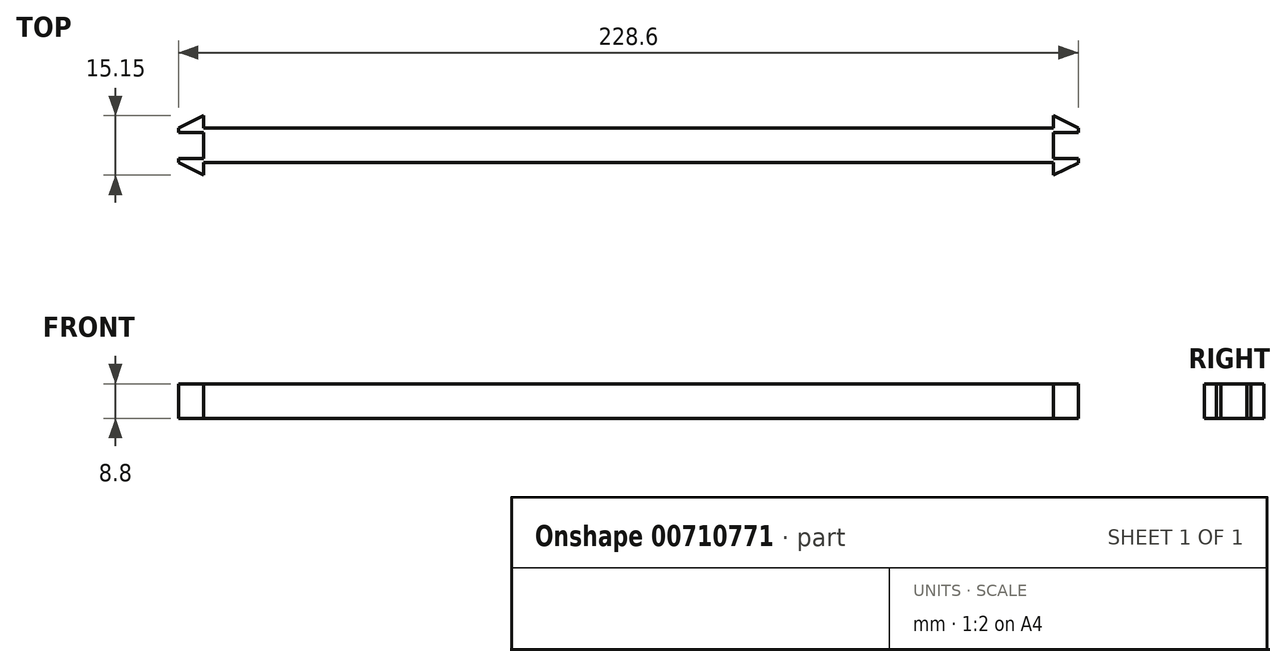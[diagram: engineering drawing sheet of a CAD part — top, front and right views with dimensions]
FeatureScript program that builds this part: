
annotation { "Feature Type Name" : "Feature", "Feature Type Description" : "" }
export const myFeature = defineFeature(function(context is Context, id is Id, definition is map)
    precondition{}
    {
        {
            var Q0;
            Q0=qCreatedBy(makeId("Top.planeOp"),FACE);
            var sketch = newSketch(context, id + "F0", { "sketchPlane" : qUnion([Q0])});
            skLineSegment(sketch, "E0", {"start": v(0, 4.46) * mm, "end": v(-107.95, 4.46) * mm});
            skLineSegment(sketch, "E1", {"start": v(-107.95, -4.34) * mm, "end": v(107.95, -4.34) * mm});
            skLineSegment(sketch, "E2", {"start": v(107.95, 0) * mm, "end": v(107.95, 0.06) * mm});
            skLineSegment(sketch, "E3", {"start": v(107.95, 4.46) * mm, "end": v(0, 4.46) * mm});
            skLineSegment(sketch, "E4", {"start": v(107.95, 4.46) * mm, "end": v(107.95, 7.63) * mm});
            skLineSegment(sketch, "E5", {"start": v(107.95, -4.34) * mm, "end": v(107.95, -7.52) * mm});
            skPoint(sketch, "E6.startSnap0", {"position": v(107.95, 0.06) * mm});
            skLineSegment(sketch, "E7", {"start": v(114.3, 0) * mm, "end": v(114.3, 4.4) * mm});
            skLineSegment(sketch, "E8", {"start": v(114.3, 4.4) * mm, "end": v(107.95, 7.63) * mm});
            skLineSegment(sketch, "E9", {"start": v(114.3, 0) * mm, "end": v(114.3, -4.4) * mm});
            skLineSegment(sketch, "E10", {"start": v(114.3, -4.4) * mm, "end": v(107.95, -7.52) * mm});
            skLineSegment(sketch, "E11", {"start": v(-107.95, 4.46) * mm, "end": v(-107.95, 7.63) * mm});
            skLineSegment(sketch, "E12", {"start": v(-107.95, -4.34) * mm, "end": v(-107.95, -7.52) * mm});
            skLineSegment(sketch, "E13", {"start": v(-114.3, 0.06) * mm, "end": v(-114.3, -4.34) * mm});
            skLineSegment(sketch, "E14", {"start": v(-114.3, -4.34) * mm, "end": v(-107.95, -7.52) * mm});
            skLineSegment(sketch, "E15", {"start": v(-114.3, 0.06) * mm, "end": v(-114.3, 4.46) * mm});
            skLineSegment(sketch, "E16", {"start": v(-114.3, 4.46) * mm, "end": v(-107.95, 7.63) * mm});
            skPoint(sketch, "E17.end.orphan", {"position": v(-114.3, 2.26) * mm});
            skPoint(sketch, "E18.end.orphan", {"position": v(-114.3, -2.14) * mm});
            skPoint(sketch, "E6.start.orphan", {"position": v(107.95, 0) * mm});
            skLineSegment(sketch, "E19", {"start": v(-107.95, 4.46) * mm, "end": v(-107.95, 3.36) * mm});
            skLineSegment(sketch, "E20", {"start": v(-107.95, -4.34) * mm, "end": v(-107.95, -3.24) * mm});
            skLineSegment(sketch, "E21", {"start": v(-107.95, 3.36) * mm, "end": v(-114.3, 3.36) * mm});
            skLineSegment(sketch, "E22", {"start": v(-107.95, -3.24) * mm, "end": v(-114.3, -3.24) * mm});
            skLineSegment(sketch, "E23", {"start": v(-114.3, -3.24) * mm, "end": v(-114.3, 3.36) * mm});
            skLineSegment(sketch, "E24", {"start": v(-107.95, 3.36) * mm, "end": v(-107.95, -3.24) * mm});
            skLineSegment(sketch, "E25", {"start": v(107.95, 4.46) * mm, "end": v(107.95, 3.36) * mm});
            skLineSegment(sketch, "E26", {"start": v(107.95, -4.34) * mm, "end": v(107.95, -3.24) * mm});
            skLineSegment(sketch, "E27", {"start": v(107.95, -3.24) * mm, "end": v(114.3, -3.24) * mm});
            skLineSegment(sketch, "E28", {"start": v(107.95, 3.36) * mm, "end": v(114.3, 3.36) * mm});
            skLineSegment(sketch, "E29", {"start": v(114.3, 3.36) * mm, "end": v(114.3, -3.24) * mm});
            skLineSegment(sketch, "E30", {"start": v(107.95, 3.36) * mm, "end": v(107.95, -3.24) * mm});
            skSolve(sketch);
        }
        {
            var Q0;
            Q0 = qSketchRegion(id + "F0", true);
            extrude(context, id + "F1", {"entities" : qUnion([Q0]), "oppositeDirection" : true, "depth" : 8.8 * mm, "offsetDistance" : 25 * mm});
        }
        {
            var Q0;
            Q0=makeQuery(id+"F0.imprint","IMPRINT",FACE,{"disambiguationData":[TD([[makeQuery(id+"F0.imprint","IMPRINT",EDGE,{"derivedFrom":sQuery(id+"F0.wireOp",EDGE,"E21")}),1.0]])]});
            extrude(context, id + "F2", {"entities" : qUnion([Q0]), "operationType" : NewBodyOperationType.REMOVE, "oppositeDirection" : true, "depth" : 25 * mm, "offsetDistance" : 25 * mm});
        }
        {
            var Q0;
            {var subQ3=sQuery(id+"F0.wireOp",EDGE,"E27");Q0=makeQuery(id+"F0.imprint","IMPRINT",FACE,{"disambiguationData":[TD([[makeQuery(id+"F0.imprint","IMPRINT",EDGE,{"derivedFrom":subQ3}),1.0]])]});}
            extrude(context, id + "F3", {"entities" : qUnion([Q0]), "operationType" : NewBodyOperationType.REMOVE, "oppositeDirection" : true, "depth" : 25 * mm, "offsetDistance" : 25 * mm});
        }
    });
